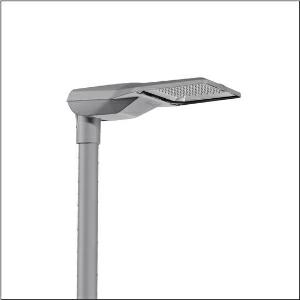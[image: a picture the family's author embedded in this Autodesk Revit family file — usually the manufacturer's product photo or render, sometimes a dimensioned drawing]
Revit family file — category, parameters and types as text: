
# Revit family: streetlight_sl_21_iq_midi___st0_8a_5xe3c21d08nb_9e73
name_source: partatom
category: Lighting Fixtures
units: mm (PartAtom-declared; Revit-internal decimal feet)

## family parameters
Cut with Voids When Loaded = No
Host = Face
Light Source = No
Part Type = Normal
Room Calculation Point = No
Round Connector Dimension = Use Diameter
Shared = No

## types (1)
- --- (1 x LED, 19210 lm, 155.5 W, 2200K)
    Apparent Load = 155 VA
    CIE Flux Codes = 41 75 97 100 100
    Color Rendering = 70
    Color Temperature = 2200K
    Default Elevation = 1800 mm
    Description = Streetlight SL 21 iQ midi, mast luminaire, primary light control with lens, of PMMA, primary optical cover: cover, of toughened safety glass, transparent, light distribution: ST0.8a, light emission: direct distribution, primary light characteristic: asymmetric, installation type: post-top, side-entry, LED, High Power LED, rated luminous flux: 19.210lm, luminous efficacy: 124lm/W, light colour: 722, colour temperature: 2200K, control: Auto-Match, Temp-Guard, Lumen-Switch, Night-Set, Smart-Wire, Light-Fading, Desk-Remote (wireless, voltage-free reading and setting of iQ features in the workshop via application-optimized NFC function/RFID function), optimised constant luminous flux control (CLO 2.0), presetting dimming linear, mains connection: 230..240V, AC, 50/60Hz, start of lifetime: 156W, end of service life: 162W, reduction: 69W, luminaire housing, of diecast aluminium, powder-coated, Siteco® metallic grey (DB 702S), corrosivity category C5 mid according to DIN EN ISO 12944, please order mast flange separately, inclination adjustable: 0°, 5°, 10°, 15°, sealing non-destructively replaceable, multi-level sealing system, length: 644mm, width: 335mm, height: 110mm, mast flange for spigot size: 42mm (side-entry): 5XC10008XM4, 60/48mm (side-entry/post-top): 5XC10108XM2, 76/60mm (side-entry/post-top): 5XC10108XM1, protection rating (complete): IP66, insulation class (complete): insulation class II (safety insulation), certification: CE, ENEC, ENEC+, VDE, impact resistance: IK09, permissible operating ambient temperature for outdoor applications: -40..+50°C, standard-compliant lighting for roads and squares, packaging unit: 1 piece

Light Distribution: ST0.8a
    Height = 111 mm
    Lamp = 1 x LED
    Lamp Light Flux = 19210 lm
    Lamp Power = 155.5 W
    Lamp count = 1
    Length = 644 mm
    Luminous efficacy = 124 lm/W
    Manufacturer = Siteco
    ModVariant = No
    Model = 5XE3C21D08NB
    Number of Poles = 1
    OnlyDefault = Yes
    Power Factor = 1
    Product Name = Streetlight SL 21 iQ midi | ST0.8a
    Product group = mast luminaire | pylon top
    ProductGroupID = 6100
    Protection Class = Protection class II
    Protection Degree = IP 66
    RLX_Detail_Level = 1
    RLX_Emergency_Light_Flux = 0 lm
    RLX_Emergency_Type = 0
    RLX_Emergency_Type_DB = No
    RlxData = <blob elided: 90793 chars, md5=a05e1c43>
    Socket = socket
    Standby Power = 0 W
    System Light Flux = 19210 lm
    System Power = 155 W
    Type Comments = factory setting: luminous flux: 100 % | dim-lin: 254 | 823 mA
    Type Image = l_1004298.jpg
    URL = http://relux.com
    VarID = @adj_101505
    Voltage = 0 V
    Weight = 0.00 kg
    Width = 336 mm

## geometry (parser evidence)
native form markers: Blend x4, Sweep x10
no freeform markers — native parametric forms only
